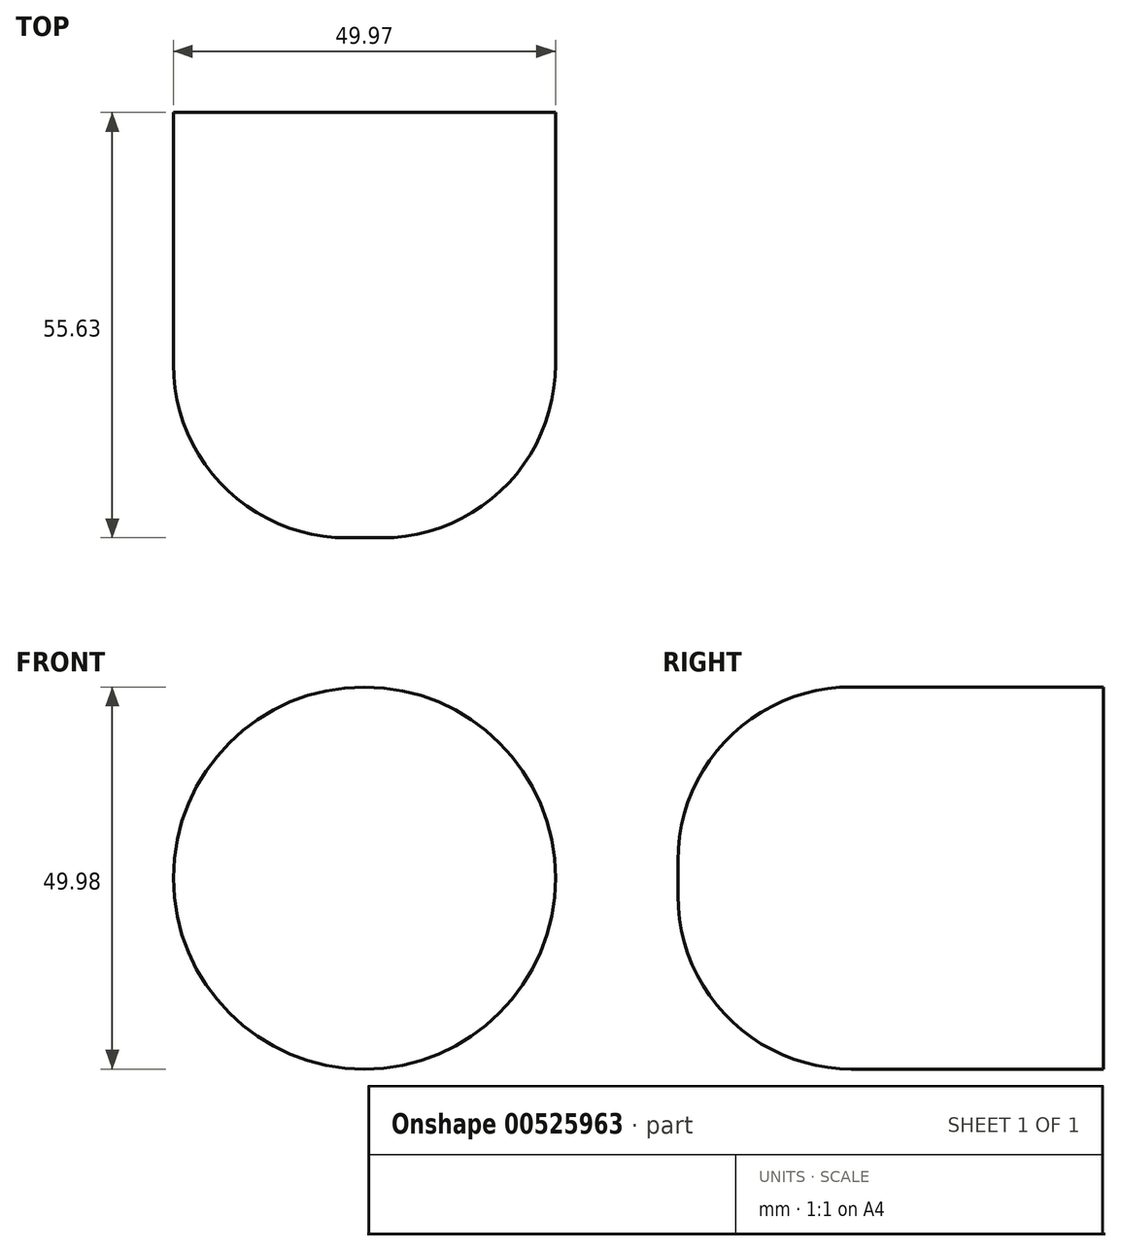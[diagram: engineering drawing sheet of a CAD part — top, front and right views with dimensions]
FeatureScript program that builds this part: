
annotation { "Feature Type Name" : "Feature", "Feature Type Description" : "" }
export const myFeature = defineFeature(function(context is Context, id is Id, definition is map)
    precondition{}
    {
        {
            var Q0;
            Q0=qCreatedBy(makeId("Front.planeOp"),FACE);
            var sketch = newSketch(context, id + "F0", { "sketchPlane" : qUnion([Q0])});
            skCircle(sketch, "E0", {"center": v(-73.45, 0) * mm, "radius": 24.99 * mm});
            skSolve(sketch);
        }
        {
            var Q0;
            Q0 = qSketchRegion(id + "F0", true);
            extrude(context, id + "F1", {"entities" : qUnion([Q0]), "oppositeDirection" : true, "depth" : 55.63 * mm, "offsetDistance" : 25.4 * mm});
        }
        {
            var Q0;
            Q0=makeQuery(id+"F1.opExtrude","CAP_EDGE",EDGE,{"disambiguationData":[OSD([sQuery(id+"F0.wireOp",EDGE,"E0")])],"isStart":true});
            fillet(context, id + "F2", {"entities" : qUnion([Q0]), "radius" : 22.7 * mm, "tangentPropagation" : true, "allowEdgeOverflow" : false});
        }
    });
